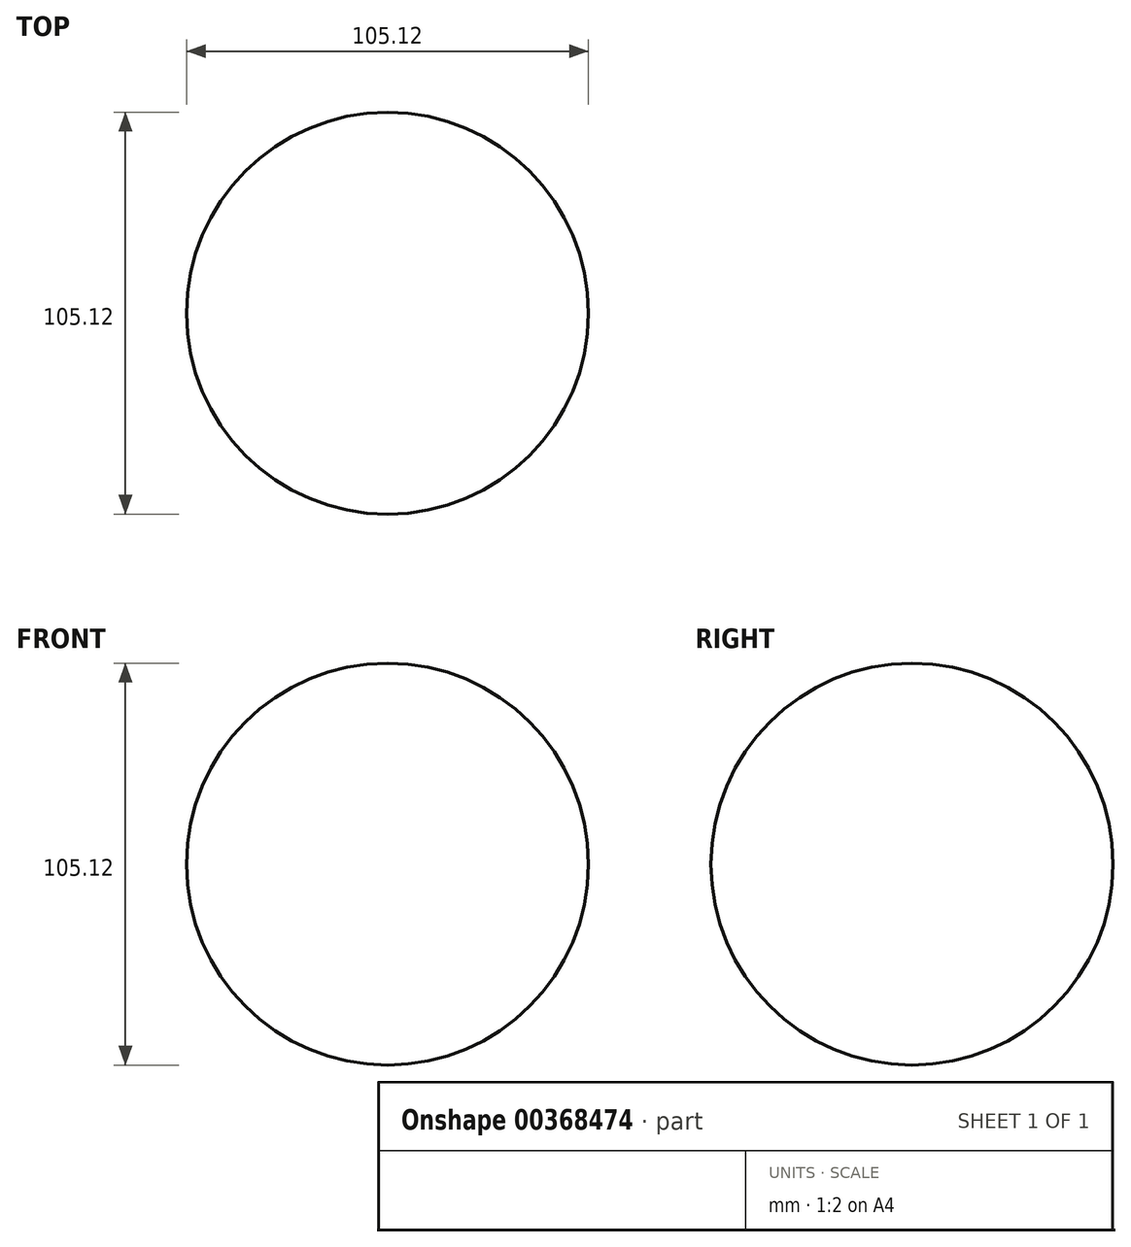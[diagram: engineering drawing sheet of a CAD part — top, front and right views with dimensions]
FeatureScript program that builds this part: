
annotation { "Feature Type Name" : "Feature", "Feature Type Description" : "" }
export const myFeature = defineFeature(function(context is Context, id is Id, definition is map)
    precondition{}
    {
        {
            var Q0;
            Q0=qCreatedBy(makeId("Top.planeOp"),FACE);
            var sketch = newSketch(context, id + "F0", { "sketchPlane" : qUnion([Q0])});
            skArc(sketch, "E0", {"start": v(0, -52.56) * mm, "mid": v(52.56, 0) * mm, "end": v(0, 52.56) * mm});
            skLineSegment(sketch, "E1", {"start": v(0, 71.47) * mm, "end": v(0, -66.36) * mm, "construction": true});
            skLineSegment(sketch, "E2", {"start": v(0, 52.56) * mm, "end": v(0, -52.56) * mm});
            skSolve(sketch);
        }
        {
            var Q0;
            Q0=makeQuery(id+"F0.imprint","IMPRINT",FACE,{"disambiguationData":[TD([[makeQuery(id+"F0.imprint","IMPRINT",EDGE,{"derivedFrom":sQuery(id+"F0.wireOp",EDGE,"E0")}),1.0]])]});
            var Q1;
            Q1=sQuery(id+"F0.wireOp",EDGE,"E1");
            revolve(context, id + "F1", {"entities" : qUnion([Q0]), "axis" : qUnion([Q1]), "revolveType" : RevolveType.FULL});
        }
    });
